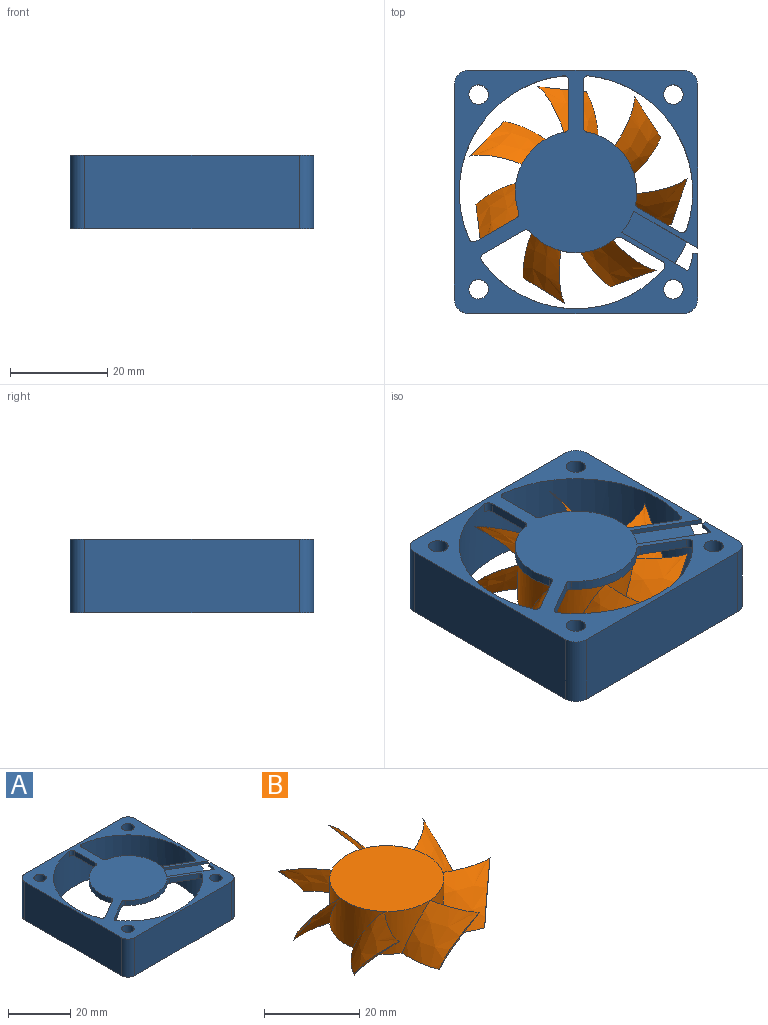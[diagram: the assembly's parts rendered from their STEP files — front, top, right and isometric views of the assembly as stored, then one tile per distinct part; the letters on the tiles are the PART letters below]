
ASSEMBLY  parts=2 mates=1
PART A: 80 faces, bbox 50x50x15.1 mm
  f0: plane 0.77x0.76mm, normal (0,0.98,0.17), area 0.6mm2, adj f5,f25,f43,f44
  f1: plane 11.23x8mm, normal (-1,0,0), area 89.9mm2, adj f41,f63,f68,f79
  f2: plane 44x15mm, normal (0,-1,0), area 660mm2, adj f16,f41,f44,f47
  f3: cylinder r=2mm len=15mm, axis (0,0,-1), area 188.5mm2, adj f41,f44
  f4: plane 13.44x10.64mm, normal (0,0,1), area 62.7mm2, adj f31,f59,f60,f61
  f5: plane 0.76x0.24mm, normal (0,1,0), area 0.2mm2, adj f0,f11,f30,f43
  f6: plane 11.34x8mm, normal (0,-1,0), area 90.7mm2, adj f26,f41,f70,f71
  f7: cylinder r=1mm len=2mm, axis (0,0,-1), area 2.5mm2, adj f21,f23,f39,f44
  f8: plane 8.51x4.91mm, normal (-0.5,-0.87,0), area 19.7mm2, adj f21,f44,f52,f54
  f9: cylinder r=1mm len=2mm, axis (0,0,-1), area 2.8mm2, adj f18,f19,f21,f44
  f10: cylinder r=3mm len=15mm, axis (0,0,1), area 70.7mm2, adj f41,f42,f44,f46
  f11: cylinder r=0.25mm len=0.25mm, axis (0,0,-1), area 0.1mm2, adj f5,f24,f25,f30
  f12: plane 11.34x8mm, normal (0,1,0), area 90.7mm2, adj f13,f14,f41,f73
  f13: plane 11.34x3.72mm, normal (0,0,-1), area 19.1mm2, adj f12,f14,f73
  f14: plane 8x3.72mm, normal (0.71,-0.71,0), area 42.1mm2, adj f12,f13,f41,f73
  f15: cylinder r=1mm len=2mm, axis (0,0,1), area 3.4mm2, adj f21,f40,f44,f49
  f16: cylinder r=3mm len=15mm, axis (0,0,1), area 70.7mm2, adj f2,f41,f43,f44
  f17: cylinder r=1mm len=2mm, axis (0,0,-1), area 2.8mm2, adj f21,f44,f50,f51
  f18: cylinder r=12.5mm len=16.42mm, axis (0,0,-1), area 43mm2, adj f9,f21,f44,f58
  f19: plane 8.31x4.8mm, normal (-0.5,0.87,0), area 19.2mm2, adj f9,f21,f44,f55
  f20: plane 9.6x2mm, normal (-1,0,0), area 19.2mm2, adj f21,f44,f56,f58
  f21: plane 44.7x39.83mm, normal (0,0,-1), area 643.5mm2, adj f7,f8,f9,f15,f17,f18,f19,f20
  f22: plane 11.34x8mm, normal (1,0,0), area 90.7mm2, adj f41,f62,f64,f78
  f23: plane 8.51x4.91mm, normal (0.5,0.87,0), area 19.7mm2, adj f7,f21,f44,f53
  f24: cylinder r=8.81mm len=3.39mm, axis (0,0,-1), area 3.5mm2, adj f11,f25,f30,f44,f59
  f25: cylinder r=0.25mm len=0.85mm, axis (0.02,0.17,-0.98), area 0.3mm2, adj f0,f11,f24,f44
  f26: cylinder r=25mm len=8mm, axis (0,0,1), area 68.2mm2, adj f6,f41,f70,f71
  f27: plane 11.34x8mm, normal (0,1,0), area 90.7mm2, adj f28,f29,f41,f76
  f28: plane 8x3.72mm, normal (-0.71,-0.71,0), area 42.1mm2, adj f27,f29,f41,f76
  f29: plane 11.34x3.72mm, normal (0,0,-1), area 19.1mm2, adj f27,f28,f76
  f30: plane 8.87x4.72mm, normal (0,0,-1), area 11.4mm2, adj f5,f11,f24,f31,f32,f34,f43,f59
  f31: cylinder r=25mm len=14.62mm, axis (0,0,1), area 218.6mm2, adj f4,f30,f32,f33,f41,f42
  f32: plane 14x3.26mm, normal (0.71,0.71,0), area 64.5mm2, adj f30,f31,f34,f41
  f33: plane 11.55x2.21mm, normal (0,0,-1), area 8.8mm2, adj f31,f42,f61
  f34: cylinder r=5mm len=14mm, axis (0,0,1), area 55mm2, adj f30,f32,f41,f43
  f35: cylinder r=2mm len=15mm, axis (0,0,-1), area 188.5mm2, adj f41,f44
  f36: cylinder r=2mm len=15mm, axis (0,0,-1), area 188.5mm2, adj f41,f44
  f37: cylinder r=2mm len=15mm, axis (0,0,-1), area 188.5mm2, adj f41,f44
  f38: cylinder r=1mm len=2mm, axis (0,0,1), area 3.4mm2, adj f21,f40,f44,f50
  f39: cylinder r=12.5mm len=14.57mm, axis (0,0,-1), area 39.2mm2, adj f7,f21,f44,f57
  f40: cylinder r=24mm len=48mm, axis (0,0,1), area 2222.1mm2, adj f15,f21,f38,f41,f44,f52,f53,f55
  f41: plane 50x50mm, normal (0,0,-1), area 465.4mm2, adj f1,f2,f3,f6,f10,f12,f14,f16
  f42: plane 33.55x15mm, normal (1,0,0), area 341.5mm2, adj f10,f31,f33,f41,f44,f61
  f43: plane 15x9.45mm, normal (1,0,0), area 17.6mm2, adj f0,f5,f16,f30,f34,f41,f44
  f44: plane 50.02x50.02mm, normal (0,0,1), area 1199.6mm2, adj f0,f2,f3,f7,f8,f9,f10,f15
  f45: plane 44x15mm, normal (-1,0,0), area 660mm2, adj f41,f44,f47,f48
  f46: plane 44x15mm, normal (0,1,0), area 660mm2, adj f10,f41,f44,f48
  f47: cylinder r=3mm len=15mm, axis (0,0,1), area 70.7mm2, adj f2,f41,f44,f45
  f48: cylinder r=3mm len=15mm, axis (0,0,1), area 70.7mm2, adj f41,f44,f45,f46
  f49: plane 9.6x2mm, normal (1,0,0), area 19.2mm2, adj f15,f21,f44,f57
  f50: plane 8.31x4.8mm, normal (0.5,-0.87,0), area 19.2mm2, adj f17,f21,f38,f44
  f51: cylinder r=12.5mm len=17.6mm, axis (0,0,-1), area 39.2mm2, adj f17,f21,f44,f54
  f52: cylinder r=1mm len=2mm, axis (0,0,1), area 3.5mm2, adj f8,f21,f40,f44
  f53: cylinder r=1mm len=2mm, axis (0,0,1), area 3.5mm2, adj f21,f23,f40,f44
  f54: cylinder r=1mm len=2mm, axis (0,0,-1), area 2.5mm2, adj f8,f21,f44,f51
  f55: cylinder r=1mm len=2mm, axis (0,0,1), area 3.4mm2, adj f19,f21,f40,f44
  f56: cylinder r=1mm len=2mm, axis (0,0,1), area 3.4mm2, adj f20,f21,f40,f44
  f57: cylinder r=1mm len=2mm, axis (0,0,-1), area 2.8mm2, adj f21,f39,f44,f49
  f58: cylinder r=1mm len=2mm, axis (0,0,-1), area 2.8mm2, adj f18,f20,f21,f44
  f59: plane 13.64x7.88mm, normal (0.5,0.87,0), area 15.8mm2, adj f4,f24,f30,f44,f60
  f60: cylinder r=12.5mm len=4.33mm, axis (0,0,-1), area 5mm2, adj f4,f44,f59,f61
  f61: plane 13.14x7.59mm, normal (-0.5,-0.87,0), area 15.2mm2, adj f4,f33,f42,f44,f60
  f62: plane 8x3.72mm, normal (-0.71,-0.71,0), area 42.1mm2, adj f22,f41,f64,f78
  f63: plane 8x3.96mm, normal (0.75,-0.66,0), area 42.1mm2, adj f1,f41,f68,f79
  f64: cylinder r=25mm len=8mm, axis (0,0,1), area 68.2mm2, adj f22,f41,f62,f78
  f65: plane 11.42x8mm, normal (0,-1,0), area 91.3mm2, adj f41,f66,f67,f77
  f66: plane 11.42x3.96mm, normal (0,0,-1), area 20.2mm2, adj f65,f67,f77
  f67: plane 8x3.96mm, normal (-0.75,0.66,0), area 42.1mm2, adj f41,f65,f66,f77
  f68: plane 11.23x3.48mm, normal (0,0,-1), area 17.8mm2, adj f1,f63,f79
  f69: cylinder r=25mm len=8mm, axis (0,0,1), area 68.2mm2, adj f41,f72,f74,f75
  f70: plane 11.34x3.72mm, normal (0,0,-1), area 19.1mm2, adj f6,f26,f71
  f71: plane 8x3.72mm, normal (0.71,0.71,0), area 42.1mm2, adj f6,f26,f41,f70
  f72: plane 11.34x3.72mm, normal (0,0,-1), area 19.1mm2, adj f69,f74,f75
  f73: cylinder r=25mm len=8mm, axis (0,0,1), area 68.2mm2, adj f12,f13,f14,f41
  f74: plane 8x3.72mm, normal (-0.71,0.71,0), area 42.1mm2, adj f41,f69,f72,f75
  f75: plane 11.34x8mm, normal (1,0,0), area 90.7mm2, adj f41,f69,f72,f74
  f76: cylinder r=25mm len=8mm, axis (0,0,1), area 68.2mm2, adj f27,f28,f29,f41
  f77: cylinder r=25mm len=8mm, axis (0,0,1), area 71.4mm2, adj f41,f65,f66,f67
  f78: plane 11.34x3.72mm, normal (0,0,-1), area 19.1mm2, adj f22,f62,f64
  f79: cylinder r=25mm len=8mm, axis (0,0,1), area 64.8mm2, adj f1,f41,f63,f68
PART B: 30 faces, bbox 43.7x44.8x11 mm
  f0: cylinder r=12mm len=15.89mm, axis (0,0,1), area 118.5mm2, adj f5,f14,f15,f17
  f1: bspline ~12.47x11.35mm, area 140.2mm2, adj f12,f21,f27
  f2: bspline ~16.61x11mm, area 139.1mm2, adj f3,f28,f29
  f3: cylinder r=12mm len=14.71mm, axis (0,0,1), area 118.5mm2, adj f2,f4,f14,f15
  f4: bspline ~13.5x11mm, area 140.2mm2, adj f3,f16,f22
  f5: bspline ~15.57x11mm, area 139.1mm2, adj f0,f23,f24
  f6: cylinder r=12mm len=14.61mm, axis (0,0,1), area 118.5mm2, adj f14,f15,f16,f23
  f7: bspline ~16.38x11mm, area 139.1mm2, adj f8,f9,f12
  f8: bspline ~16.1x11mm, area 140.2mm2, adj f7,f9,f10
  f9: plane 11x9.01mm, normal (-0.9,-0.43,0), area 3.7mm2, adj f7,f8
  f10: cylinder r=12mm len=16.27mm, axis (0,0,1), area 118.5mm2, adj f8,f14,f15,f18
  f11: cylinder r=12mm len=12.65mm, axis (0,0,1), area 118.5mm2, adj f14,f15,f19,f25
  f12: cylinder r=12mm len=12.79mm, axis (0,0,1), area 118.5mm2, adj f1,f7,f14,f15
  f13: cylinder r=12mm len=15.84mm, axis (0,0,1), area 118.5mm2, adj f14,f15,f27,f28
  f14: plane 24x24mm, normal (0,0,1), area 452.4mm2, adj f0,f3,f6,f10,f11,f12,f13
  f15: plane 24x24mm, normal (0,0,-1), area 452.4mm2, adj f0,f3,f6,f10,f11,f12,f13
  f16: bspline ~13.5x11mm, area 139.1mm2, adj f4,f6,f22
  f17: bspline ~15.14x11mm, area 140.2mm2, adj f0,f20,f25
  f18: bspline ~14.61x11mm, area 139.1mm2, adj f10,f19,f26
  f19: bspline ~14.13x11mm, area 140.2mm2, adj f11,f18,f26
  f20: plane 11x9.75mm, normal (-0.22,0.97,0), area 3.7mm2, adj f17,f25
  f21: plane 11x9.75mm, normal (-0.22,-0.97,0), area 3.7mm2, adj f1,f27
  f22: plane 11x10mm, normal (1,0,0), area 3.7mm2, adj f4,f16
  f23: bspline ~15.57x11mm, area 140.2mm2, adj f5,f6,f24
  f24: plane 11x7.82mm, normal (0.62,0.78,0), area 3.7mm2, adj f5,f23
  f25: bspline ~15.14x11mm, area 139.1mm2, adj f11,f17,f20
  f26: plane 11x9.01mm, normal (-0.9,0.43,0), area 3.7mm2, adj f18,f19
  f27: bspline ~12.47x11.35mm, area 139.1mm2, adj f1,f13,f21
  f28: bspline ~16.24x11mm, area 140.2mm2, adj f2,f13,f29
  f29: plane 11x7.82mm, normal (0.62,-0.78,0), area 3.7mm2, adj f2,f28
PLACE A at identity fixed
PLACE B rot(axis=(0,0,-1),70.1deg) t=(0,0,2)mm
MATE revolute B.f0 <-> A.f40  axis (0,0,1) through (0,0,13)mm
